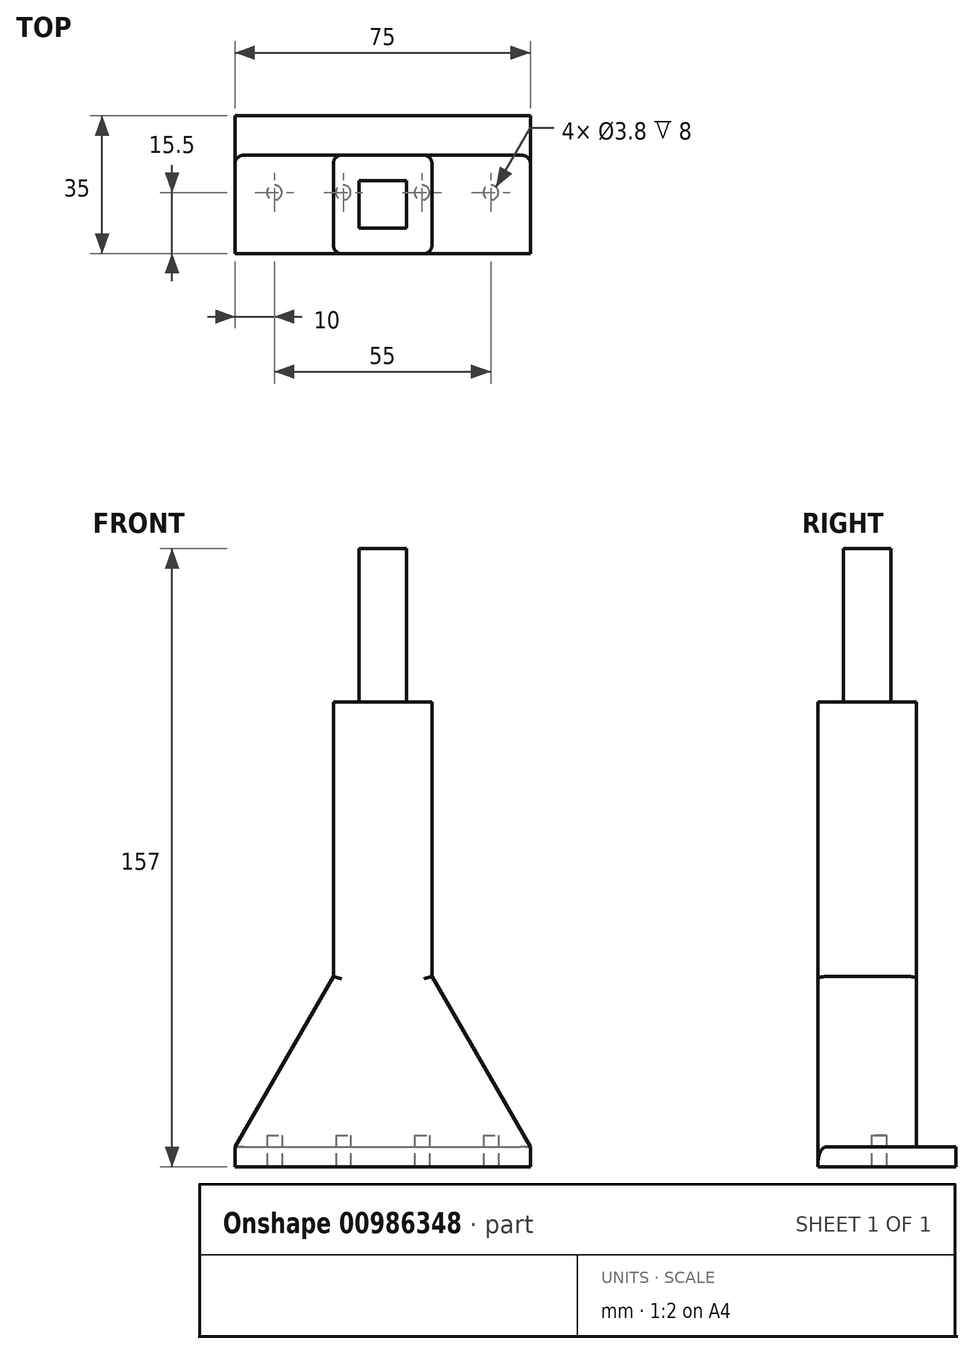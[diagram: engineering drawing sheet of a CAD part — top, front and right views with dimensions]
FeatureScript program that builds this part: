
annotation { "Feature Type Name" : "Feature", "Feature Type Description" : "" }
export const myFeature = defineFeature(function(context is Context, id is Id, definition is map)
    precondition{}
    {
        {
            var Q0;
            Q0=qCreatedBy(makeId("Top.planeOp"),FACE);
            var sketch = newSketch(context, id + "F0", { "sketchPlane" : qUnion([Q0])});
            skLineSegment(sketch, "E0.bottom", {"start": v(0, 0) * mm, "end": v(75, 0) * mm});
            skLineSegment(sketch, "E0.top", {"start": v(0, 35) * mm, "end": v(75, 35) * mm});
            skLineSegment(sketch, "E0.left", {"start": v(0, 0) * mm, "end": v(0, 35) * mm});
            skLineSegment(sketch, "E0.right", {"start": v(75, 0) * mm, "end": v(75, 35) * mm});
            skSolve(sketch);
        }
        {
            var Q0;
            Q0=qSketchRegion(id+"F0",true);
            extrude(context, id + "F1", {"entities" : qUnion([Q0]), "depth" : 5 * mm});
        }
        {
            var Q0;
            Q0=makeQuery(id+"F1.opExtrude","SWEPT_FACE",FACE,{"disambiguationData":[OSD([sQuery(id+"F0.wireOp",EDGE,"E0.bottom")])]});
            var sketch = newSketch(context, id + "F2", { "sketchPlane" : qUnion([Q0])});
            skLineSegment(sketch, "E1", {"start": v(0, 5) * mm, "end": v(25, 5) * mm});
            skLineSegment(sketch, "E2", {"start": v(25, 5) * mm, "end": v(25, 118) * mm});
            skLineSegment(sketch, "E3", {"start": v(25, 118) * mm, "end": v(50, 118) * mm});
            skLineSegment(sketch, "E4", {"start": v(50, 118) * mm, "end": v(50, 5) * mm});
            skLineSegment(sketch, "E5", {"start": v(50, 5) * mm, "end": v(25, 5) * mm});
            skLineSegment(sketch, "E6", {"start": v(50, 5) * mm, "end": v(75, 5) * mm});
            skLineSegment(sketch, "E7", {"start": v(75, 5) * mm, "end": v(50, 48.3) * mm});
            skLineSegment(sketch, "E8", {"start": v(0, 5) * mm, "end": v(25, 48.3) * mm});
            skSolve(sketch);
        }
        {
            var Q0;
            Q0=qSketchRegion(id+"F2",true);
            extrude(context, id + "F3", {"entities" : qUnion([Q0]), "operationType" : NewBodyOperationType.ADD, "oppositeDirection" : true, "depth" : 25 * mm});
        }
        {
            var Q0;
            Q0=makeQuery(id+"F3.opExtrude","SWEPT_FACE",FACE,{"disambiguationData":[OSD([sQuery(id+"F2.wireOp",EDGE,"E3")])]});
            var sketch = newSketch(context, id + "F4", { "sketchPlane" : qUnion([Q0])});
            skLineSegment(sketch, "E9.bottom", {"start": v(31.5, 6.5) * mm, "end": v(43.5, 6.5) * mm});
            skLineSegment(sketch, "E9.top", {"start": v(31.5, 18.5) * mm, "end": v(43.5, 18.5) * mm});
            skLineSegment(sketch, "E9.left", {"start": v(31.5, 6.5) * mm, "end": v(31.5, 18.5) * mm});
            skLineSegment(sketch, "E9.right", {"start": v(43.5, 6.5) * mm, "end": v(43.5, 18.5) * mm});
            skPoint(sketch, "E9.middle", {"position": v(37.5, 12.5) * mm});
            skPoint(sketch, "E9.middle.positionSnap0", {"position": v(50, 12.5) * mm});
            skPoint(sketch, "E9.middle.positionSnap1", {"position": v(37.5, 0) * mm});
            skPoint(sketch, "E9.centerSnap0", {"position": v(50, 12.5) * mm});
            skPoint(sketch, "E9.centerSnap1", {"position": v(37.5, 0) * mm});
            skSolve(sketch);
        }
        {
            var Q0;
            Q0=qSketchRegion(id+"F4",true);
            extrude(context, id + "F5", {"entities" : qUnion([Q0]), "operationType" : NewBodyOperationType.ADD, "depth" : 39 * mm});
        }
        {
            var Q0;
            Q0=makeQuery(id+"F1.opExtrude","CAP_FACE",FACE,{"disambiguationData":[OSD([sQuery(id+"F0.wireOp",EDGE,"E0.bottom"),sQuery(id+"F0.wireOp",EDGE,"E0.top"),sQuery(id+"F0.wireOp",EDGE,"E0.left"),sQuery(id+"F0.wireOp",EDGE,"E0.right")])],"isStart":true});
            var sketch = newSketch(context, id + "F6", { "sketchPlane" : qUnion([Q0])});
            skSolve(sketch);
        }
        {
            var Q0;
            Q0=makeQuery(id+"F6.imprint","IMPRINT",FACE,{"disambiguationData":[TD([[makeQuery(id+"F6.imprint","IMPRINT",EDGE,{"derivedFrom":makeQuery(id+"F1.opExtrude","CAP_EDGE",EDGE,{"disambiguationData":[OSD([sQuery(id+"F0.wireOp",EDGE,"E0.bottom")])],"isStart":true})}),-1.0]])]});
            var sketch = newSketch(context, id + "F7", { "sketchPlane" : qUnion([Q0])});
            skLineSegment(sketch, "E10", {"start": v(0, 0) * mm, "end": v(0, -15.5) * mm});
            skLineSegment(sketch, "E11", {"start": v(0, -15.5) * mm, "end": v(10, -15.5) * mm});
            skCircle(sketch, "E12", {"center": v(10, -15.5) * mm, "radius": 1.9 * mm});
            skLineSegment(sketch, "E13", {"start": v(10, -15.5) * mm, "end": v(27.5, -15.5) * mm});
            skCircle(sketch, "E14", {"center": v(27.5, -15.5) * mm, "radius": 1.9 * mm});
            skLineSegment(sketch, "E15", {"start": v(0, 0) * mm, "end": v(75, 0) * mm});
            skLineSegment(sketch, "E16", {"start": v(37.5, 0) * mm, "end": v(37.5, -10.06) * mm});
            skCircle(sketch, "E17.MirrorC", {"center": v(47.5, -15.5) * mm, "radius": 1.9 * mm});
            skCircle(sketch, "E18.MirrorC", {"center": v(65, -15.5) * mm, "radius": 1.9 * mm});
            skSolve(sketch);
        }
        {
            var Q0;
            Q0=qSketchRegion(id+"F7",true);
            extrude(context, id + "F8", {"entities" : qUnion([Q0]), "operationType" : NewBodyOperationType.REMOVE, "oppositeDirection" : true, "depth" : 8 * mm});
        }
        {
            var Q0;
            Q0=makeQuery(id+"F3.opExtrude","CAP_EDGE",EDGE,{"disambiguationData":[OSD([sQuery(id+"F2.wireOp",EDGE,"E4")])],"isStart":true});
            var Q1;
            Q1=makeQuery(id+"F3.opExtrude","CAP_EDGE",EDGE,{"disambiguationData":[OSD([sQuery(id+"F2.wireOp",EDGE,"E4")])],"isStart":false});
            var Q2;
            Q2=makeQuery(id+"F3.opExtrude","CAP_EDGE",EDGE,{"disambiguationData":[OSD([sQuery(id+"F2.wireOp",EDGE,"E2")])],"isStart":false});
            var Q3;
            Q3=makeQuery(id+"F3.opExtrude","CAP_EDGE",EDGE,{"disambiguationData":[OSD([sQuery(id+"F2.wireOp",EDGE,"E2")])],"isStart":true});
            var Q4;
            Q4=makeQuery(id+"F3.opExtrude","CAP_EDGE",EDGE,{"disambiguationData":[OSD([sQuery(id+"F2.wireOp",EDGE,"E8")])],"isStart":true});
            var Q5;
            Q5=makeQuery(id+"F3.opExtrude","CAP_EDGE",EDGE,{"disambiguationData":[OSD([sQuery(id+"F2.wireOp",EDGE,"E7")])],"isStart":true});
            var Q6;
            Q6=makeQuery(id+"F3.opExtrude","CAP_EDGE",EDGE,{"disambiguationData":[OSD([sQuery(id+"F2.wireOp",EDGE,"E7")])],"isStart":false});
            var Q7;
            Q7=makeQuery(id+"F3.opExtrude","CAP_EDGE",EDGE,{"disambiguationData":[OSD([sQuery(id+"F2.wireOp",EDGE,"E8")])],"isStart":false});
            fillet(context, id + "F9", {"entities" : qUnion([Q0, Q1, Q2, Q3, Q4, Q5, Q6, Q7]), "radius" : 2 * mm, "tangentPropagation" : true, "allowEdgeOverflow" : false});
        }
    });
